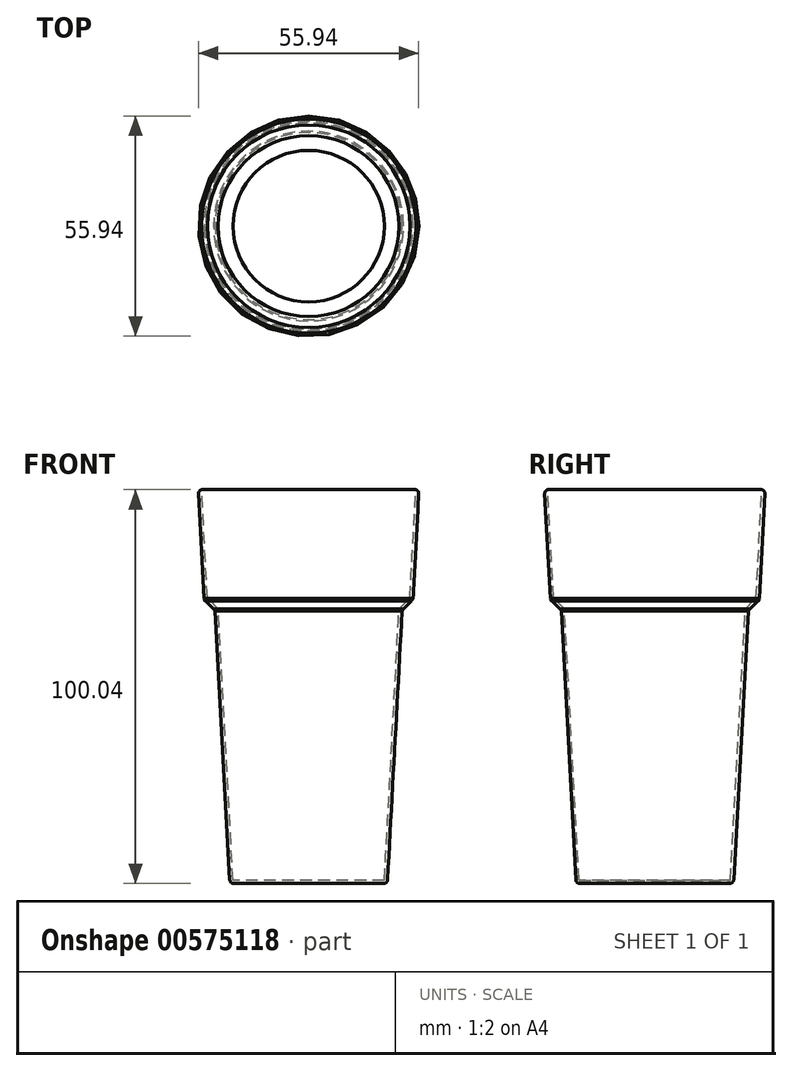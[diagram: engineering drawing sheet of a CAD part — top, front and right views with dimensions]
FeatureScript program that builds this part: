
annotation { "Feature Type Name" : "Feature", "Feature Type Description" : "" }
export const myFeature = defineFeature(function(context is Context, id is Id, definition is map)
    precondition{}
    {
        {
            var Q0;
            Q0=qCreatedBy(makeId("Front.planeOp"),FACE);
            var sketch = newSketch(context, id + "F0", { "sketchPlane" : qUnion([Q0])});
            skLineSegment(sketch, "E0", {"start": v(-25.02, 85.68) * mm, "end": v(-23.52, 57.87) * mm});
            skLineSegment(sketch, "E1", {"start": v(-17, -14.32) * mm, "end": v(3, -14.32) * mm});
            skLineSegment(sketch, "E2", {"start": v(3, 70.4) * mm, "end": v(3, -37.08) * mm, "construction": true});
            skLineSegment(sketch, "E3", {"start": v(-20.76, 55.12) * mm, "end": v(-17, -14.32) * mm});
            skLineSegment(sketch, "E4", {"start": v(-23.52, 57.87) * mm, "end": v(-20.76, 55.12) * mm});
            skLineSegment(sketch, "E5.0", {"start": v(-16.24, -13.52) * mm, "end": v(3, -13.52) * mm});
            skLineSegment(sketch, "E5.1", {"start": v(-19.98, 55.47) * mm, "end": v(-16.24, -13.52) * mm});
            skLineSegment(sketch, "E5.2", {"start": v(-22.73, 58.22) * mm, "end": v(-19.98, 55.47) * mm});
            skLineSegment(sketch, "E5.3", {"start": v(-24.22, 85.72) * mm, "end": v(-22.73, 58.22) * mm});
            skLineSegment(sketch, "E6", {"start": v(-25.02, 85.68) * mm, "end": v(-24.22, 85.72) * mm});
            skLineSegment(sketch, "E7", {"start": v(3, -13.52) * mm, "end": v(3, -14.32) * mm});
            skSolve(sketch);
        }
        {
            var Q0;
            Q0=makeQuery(id+"F0.imprint","IMPRINT",FACE,{"disambiguationData":[TD([[makeQuery(id+"F0.imprint","IMPRINT",EDGE,{"derivedFrom":sQuery(id+"F0.wireOp",EDGE,"E0")}),1.0]])]});
            var Q1;
            Q1=sQuery(id+"F0.wireOp",EDGE,"E5.3");
            var Q2;
            Q2=sQuery(id+"F0.wireOp",EDGE,"E5.2");
            var Q3;
            Q3=sQuery(id+"F0.wireOp",EDGE,"E0");
            var Q4;
            Q4=sQuery(id+"F0.wireOp",EDGE,"E5.0");
            var Q5;
            Q5=sQuery(id+"F0.wireOp",EDGE,"E4");
            var Q6;
            Q6=sQuery(id+"F0.wireOp",EDGE,"E5.1");
            var Q7;
            Q7=sQuery(id+"F0.wireOp",EDGE,"E1");
            var Q8;
            Q8=sQuery(id+"F0.wireOp",EDGE,"E3");
            var Q9;
            Q9=sQuery(id+"F0.wireOp",EDGE,"E6");
            var Q10;
            Q10=sQuery(id+"F0.wireOp",EDGE,"E7");
            var Q11;
            Q11=sQuery(id+"F0.wireOp",EDGE,"E2");
            revolve(context, id + "F1", {"entities" : qUnion([Q0]), "surfaceEntities" : qUnion([Q1, Q2, Q3, Q4, Q5, Q6, Q7, Q8, Q9, Q10]), "axis" : qUnion([Q11]), "revolveType" : RevolveType.FULL});
        }
        {
            var Q0;
            Q0=makeQuery(id+"F1.opRevolve","SWEPT_EDGE",EDGE,{"disambiguationData":[OSD([sQuery(id+"F0.wireOp",EDGE,"E0"),sQuery(id+"F0.wireOp",EDGE,"E6")])]});
            var Q1;
            Q1=makeQuery(id+"F1.opRevolve","SWEPT_EDGE",EDGE,{"disambiguationData":[OSD([sQuery(id+"F0.wireOp",EDGE,"E1"),sQuery(id+"F0.wireOp",EDGE,"E3")])]});
            fillet(context, id + "F2", {"entities" : qUnion([Q0, Q1]), "radius" : 1 * mm, "tangentPropagation" : true, "allowEdgeOverflow" : false});
        }
        {
            var Q0;
            Q0=makeQuery(id+"F1.opRevolve","SWEPT_EDGE",EDGE,{"disambiguationData":[OSD([sQuery(id+"F0.wireOp",EDGE,"E0"),sQuery(id+"F0.wireOp",EDGE,"E4")])]});
            var Q1;
            Q1=makeQuery(id+"F1.opRevolve","SWEPT_FACE",FACE,{"disambiguationData":[OSD([sQuery(id+"F0.wireOp",EDGE,"E4")])]});
            chamfer(context, id + "F3", {"entities" : qUnion([Q0, Q1]), "chamferType" : ChamferType.TWO_OFFSETS, "width1" : .25 * mm, "oppositeDirection" : false, "width2" : .5 * mm, "tangentPropagation" : true});
        }
    });
